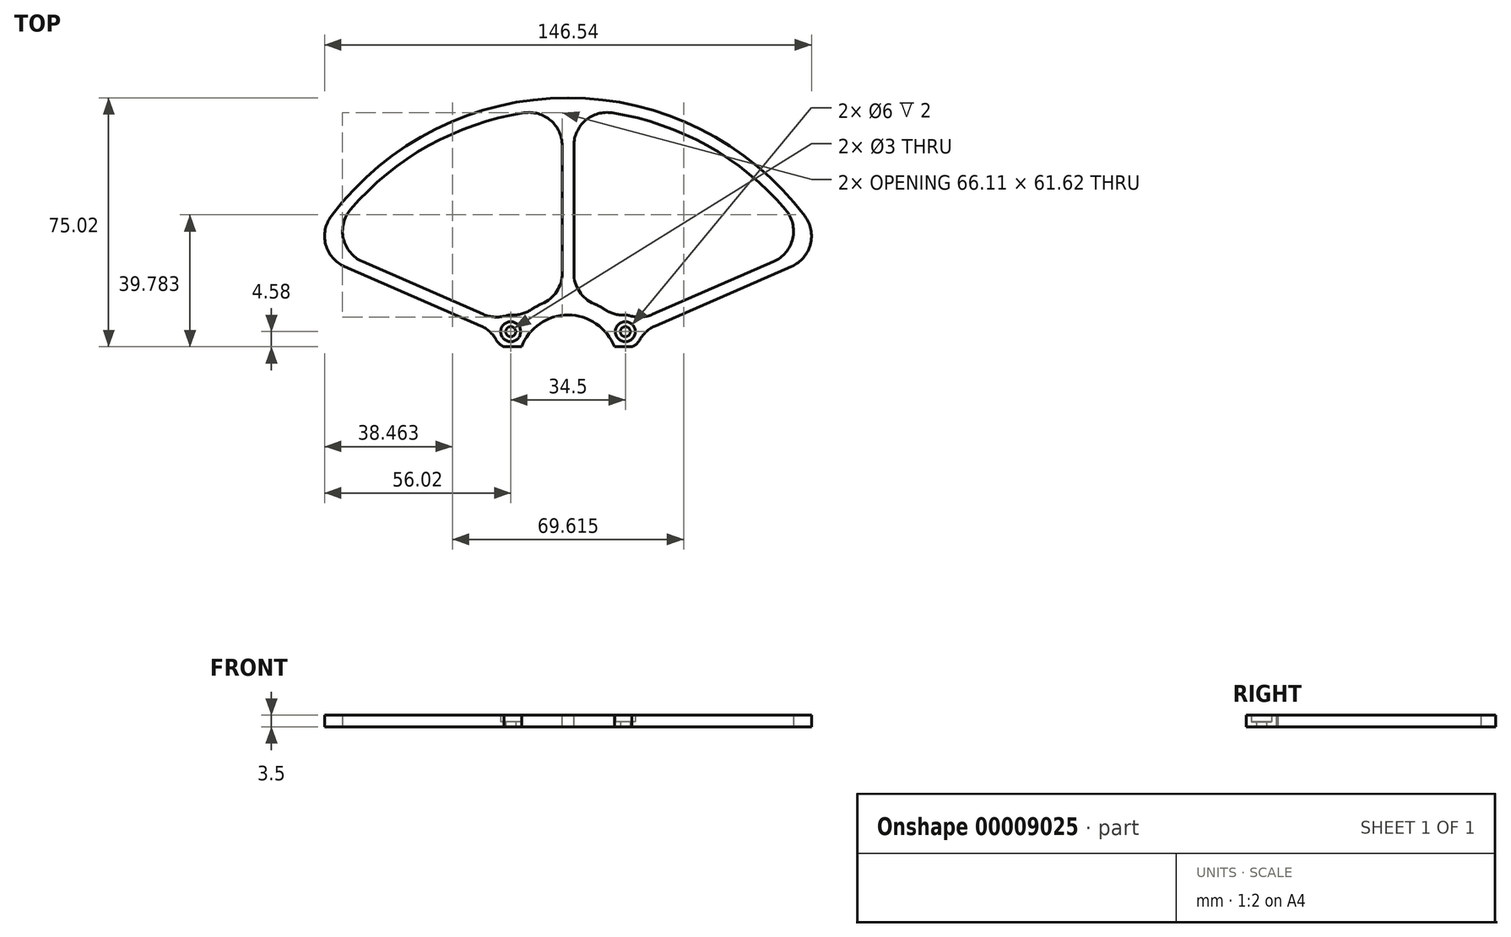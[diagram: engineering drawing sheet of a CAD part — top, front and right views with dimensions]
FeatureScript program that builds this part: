
annotation { "Feature Type Name" : "Feature", "Feature Type Description" : "" }
export const myFeature = defineFeature(function(context is Context, id is Id, definition is map)
    precondition{}
    {
        {
            var Q0;
            Q0=qCreatedBy(makeId("Top.planeOp"),FACE);
            var sketch = newSketch(context, id + "F0", { "sketchPlane" : qUnion([Q0])});
            skLineSegment(sketch, "E0", {"start": v(-17.25, 0) * mm, "end": v(17.25, 0) * mm});
            skCircle(sketch, "E1", {"center": v(17.25, 0) * mm, "radius": 1.5 * mm});
            skCircle(sketch, "E2", {"center": v(-17.25, 0) * mm, "radius": 1.5 * mm});
            skCircle(sketch, "E3", {"center": v(-17.25, 0) * mm, "radius": 3 * mm});
            skCircle(sketch, "E4", {"center": v(17.25, 0) * mm, "radius": 3 * mm});
            skCircle(sketch, "E5", {"center": v(0, -10) * mm, "radius": 15 * mm});
            skLineSegment(sketch, "E6", {"start": v(0, -10) * mm, "end": v(0, 0) * mm, "construction": true});
            skArc(sketch, "E7", {"start": v(-19.25, -4.58) * mm, "mid": v(0, -30) * mm, "end": v(19.25, -4.58) * mm});
            skArc(sketch, "E8", {"start": v(-14.27, 4.01) * mm, "mid": v(-21.58, 2.5) * mm, "end": v(-19.25, -4.58) * mm});
            skArc(sketch, "E9", {"start": v(19.25, -4.58) * mm, "mid": v(21.58, 2.5) * mm, "end": v(14.27, 4.01) * mm});
            skArc(sketch, "E10.trimOffspring", {"start": v(14.27, 4.01) * mm, "mid": v(0, 10) * mm, "end": v(-14.27, 4.01) * mm});
            skLineSegment(sketch, "E11", {"start": v(-22.25, 0) * mm, "end": v(-78.03, 24.35) * mm});
            skLineSegment(sketch, "E12", {"start": v(22.25, 0) * mm, "end": v(78.03, 24.35) * mm});
            skLineSegment(sketch, "E13", {"start": v(-21.02, 3.28) * mm, "end": v(-73.26, 26.08) * mm});
            skLineSegment(sketch, "E14", {"start": v(21.02, 3.28) * mm, "end": v(73.26, 26.08) * mm});
            skLineSegment(sketch, "E15", {"start": v(-21.02, 3.28) * mm, "end": v(-22.42, 0.07) * mm, "construction": true});
            skLineSegment(sketch, "E16", {"start": v(21.02, 3.28) * mm, "end": v(22.42, 0.07) * mm, "construction": true});
            skLineSegment(sketch, "E17", {"start": v(-73.26, 26.08) * mm, "end": v(73.26, 26.08) * mm, "construction": true});
            skArc(sketch, "E18", {"start": v(78.03, 24.35) * mm, "mid": v(0, 70.44) * mm, "end": v(-78.03, 24.35) * mm});
            skArc(sketch, "E19", {"start": v(73.26, 26.08) * mm, "mid": v(0, 66.94) * mm, "end": v(-73.26, 26.08) * mm});
            skLineSegment(sketch, "E20", {"start": v(0, 66.94) * mm, "end": v(0, 70.44) * mm, "construction": true});
            skLineSegment(sketch, "E21", {"start": v(-1.75, 66.92) * mm, "end": v(-1.75, 9.92) * mm});
            skLineSegment(sketch, "E22", {"start": v(1.75, 9.92) * mm, "end": v(1.75, 66.92) * mm});
            skLineSegment(sketch, "E23", {"start": v(-1.75, 38.42) * mm, "end": v(1.75, 38.42) * mm, "construction": true});
            skPoint(sketch, "E24", {"position": v(0, 9.92) * mm});
            skLineSegment(sketch, "E25", {"start": v(-19.25, -4.58) * mm, "end": v(19.25, -4.58) * mm});
            skLineSegment(sketch, "E26", {"start": v(-73.26, 26.08) * mm, "end": v(-74.66, 22.87) * mm, "construction": true});
            skLineSegment(sketch, "E27", {"start": v(73.26, 26.08) * mm, "end": v(74.66, 22.87) * mm, "construction": true});
            skLineSegment(sketch, "E28", {"start": v(-73.96, 24.48) * mm, "end": v(-77.17, 25.88) * mm, "construction": true});
            skLineSegment(sketch, "E29", {"start": v(73.96, 24.48) * mm, "end": v(77.17, 25.88) * mm, "construction": true});
            skSolve(sketch);
        }
        {
            var Q0;
            Q0=makeQuery(id+"F0.imprint","IMPRINT",FACE,{"disambiguationData":[TD([[makeQuery(id+"F0.imprint","IMPRINT",EDGE,{"derivedFrom":sQuery(id+"F0.wireOp",EDGE,"E3")}),-1.0]])]});
            var Q1;
            {var subQ6=sQuery(id+"F0.wireOp",EDGE,"E11");Q1=makeQuery(id+"F0.imprint","IMPRINT",FACE,{"disambiguationData":[TD([[makeQuery(id+"F0.imprint","IMPRINT",EDGE,{"derivedFrom":subQ6}),-1.0]])]});}
            var Q2;
            {var subQ1=sQuery(id+"F0.wireOp",EDGE,"E21");Q2=makeQuery(id+"F0.imprint","IMPRINT",FACE,{"disambiguationData":[TD([[makeQuery(id+"F0.imprint","IMPRINT",EDGE,{"derivedFrom":subQ1}),1.0]])]});}
            extrude(context, id + "F1", {"entities" : qUnion([Q0, Q1, Q2]), "depth" : 3.5 * mm});
        }
        {
            var Q0;
            Q0=makeQuery(id+"F0.imprint","IMPRINT",FACE,{"disambiguationData":[TD([[makeQuery(id+"F0.imprint","IMPRINT",EDGE,{"derivedFrom":sQuery(id+"F0.wireOp",EDGE,"E2")}),-1.0]])]});
            var Q1;
            Q1=makeQuery(id+"F0.imprint","IMPRINT",FACE,{"disambiguationData":[TD([[makeQuery(id+"F0.imprint","IMPRINT",EDGE,{"derivedFrom":sQuery(id+"F0.wireOp",EDGE,"E1")}),-1.0]])]});
            extrude(context, id + "F2", {"entities" : qUnion([Q0, Q1]), "operationType" : NewBodyOperationType.ADD, "depth" : 1.5 * mm});
        }
        {
            var Q0;
            Q0=makeQuery(id+"F1.opExtrude","SWEPT_EDGE",EDGE,{"disambiguationData":[OSD([sQuery(id+"F0.wireOp",EDGE,"E13"),sQuery(id+"F0.wireOp",EDGE,"E19")])]});
            var Q1;
            Q1=makeQuery(id+"F1.opExtrude","SWEPT_EDGE",EDGE,{"disambiguationData":[OSD([sQuery(id+"F0.wireOp",EDGE,"E19"),sQuery(id+"F0.wireOp",EDGE,"E21")])]});
            var Q2;
            Q2=makeQuery(id+"F1.opExtrude","SWEPT_EDGE",EDGE,{"disambiguationData":[OSD([sQuery(id+"F0.wireOp",EDGE,"E19"),sQuery(id+"F0.wireOp",EDGE,"E22")])]});
            var Q3;
            Q3=makeQuery(id+"F1.opExtrude","SWEPT_EDGE",EDGE,{"disambiguationData":[OSD([sQuery(id+"F0.wireOp",EDGE,"E14"),sQuery(id+"F0.wireOp",EDGE,"E19")])]});
            var Q4;
            Q4=makeQuery(id+"F1.opExtrude","SWEPT_EDGE",EDGE,{"disambiguationData":[OSD([sQuery(id+"F0.wireOp",EDGE,"E10.trimOffspring"),sQuery(id+"F0.wireOp",EDGE,"E22")])]});
            var Q5;
            Q5=makeQuery(id+"F1.opExtrude","SWEPT_EDGE",EDGE,{"disambiguationData":[OSD([sQuery(id+"F0.wireOp",EDGE,"E10.trimOffspring"),sQuery(id+"F0.wireOp",EDGE,"E21")])]});
            var Q6;
            Q6=makeQuery(id+"F1.opExtrude","SWEPT_EDGE",EDGE,{"disambiguationData":[OSD([sQuery(id+"F0.wireOp",EDGE,"E9"),sQuery(id+"F0.wireOp",EDGE,"E14")])]});
            var Q7;
            Q7=makeQuery(id+"F1.opExtrude","SWEPT_EDGE",EDGE,{"disambiguationData":[OSD([sQuery(id+"F0.wireOp",EDGE,"E9"),sQuery(id+"F0.wireOp",EDGE,"E12")])]});
            var Q8;
            Q8=makeQuery(id+"F1.opExtrude","SWEPT_EDGE",EDGE,{"disambiguationData":[OSD([sQuery(id+"F0.wireOp",EDGE,"E8"),sQuery(id+"F0.wireOp",EDGE,"E13")])]});
            var Q9;
            Q9=makeQuery(id+"F1.opExtrude","SWEPT_EDGE",EDGE,{"disambiguationData":[OSD([sQuery(id+"F0.wireOp",EDGE,"E8"),sQuery(id+"F0.wireOp",EDGE,"E11")])]});
            var Q10;
            Q10=makeQuery(id+"F1.opExtrude","SWEPT_EDGE",EDGE,{"disambiguationData":[OSD([sQuery(id+"F0.wireOp",EDGE,"E11"),sQuery(id+"F0.wireOp",EDGE,"E18")])]});
            var Q11;
            Q11=makeQuery(id+"F1.opExtrude","SWEPT_EDGE",EDGE,{"disambiguationData":[OSD([sQuery(id+"F0.wireOp",EDGE,"E12"),sQuery(id+"F0.wireOp",EDGE,"E18")])]});
            var Q12;
            Q12=makeQuery(id+"F1.opExtrude","SWEPT_EDGE",EDGE,{"disambiguationData":[OSD([sQuery(id+"F0.wireOp",EDGE,"E8"),sQuery(id+"F0.wireOp",EDGE,"E10.trimOffspring")])]});
            var Q13;
            Q13=makeQuery(id+"F1.opExtrude","SWEPT_EDGE",EDGE,{"disambiguationData":[OSD([sQuery(id+"F0.wireOp",EDGE,"E9"),sQuery(id+"F0.wireOp",EDGE,"E10.trimOffspring")])]});
            fillet(context, id + "F3", {"entities" : qUnion([Q0, Q1, Q2, Q3, Q4, Q5, Q6, Q7, Q8, Q9, Q10, Q11, Q12, Q13]), "radius" : 10 * mm, "tangentPropagation" : true, "allowEdgeOverflow" : false});
        }
    });
